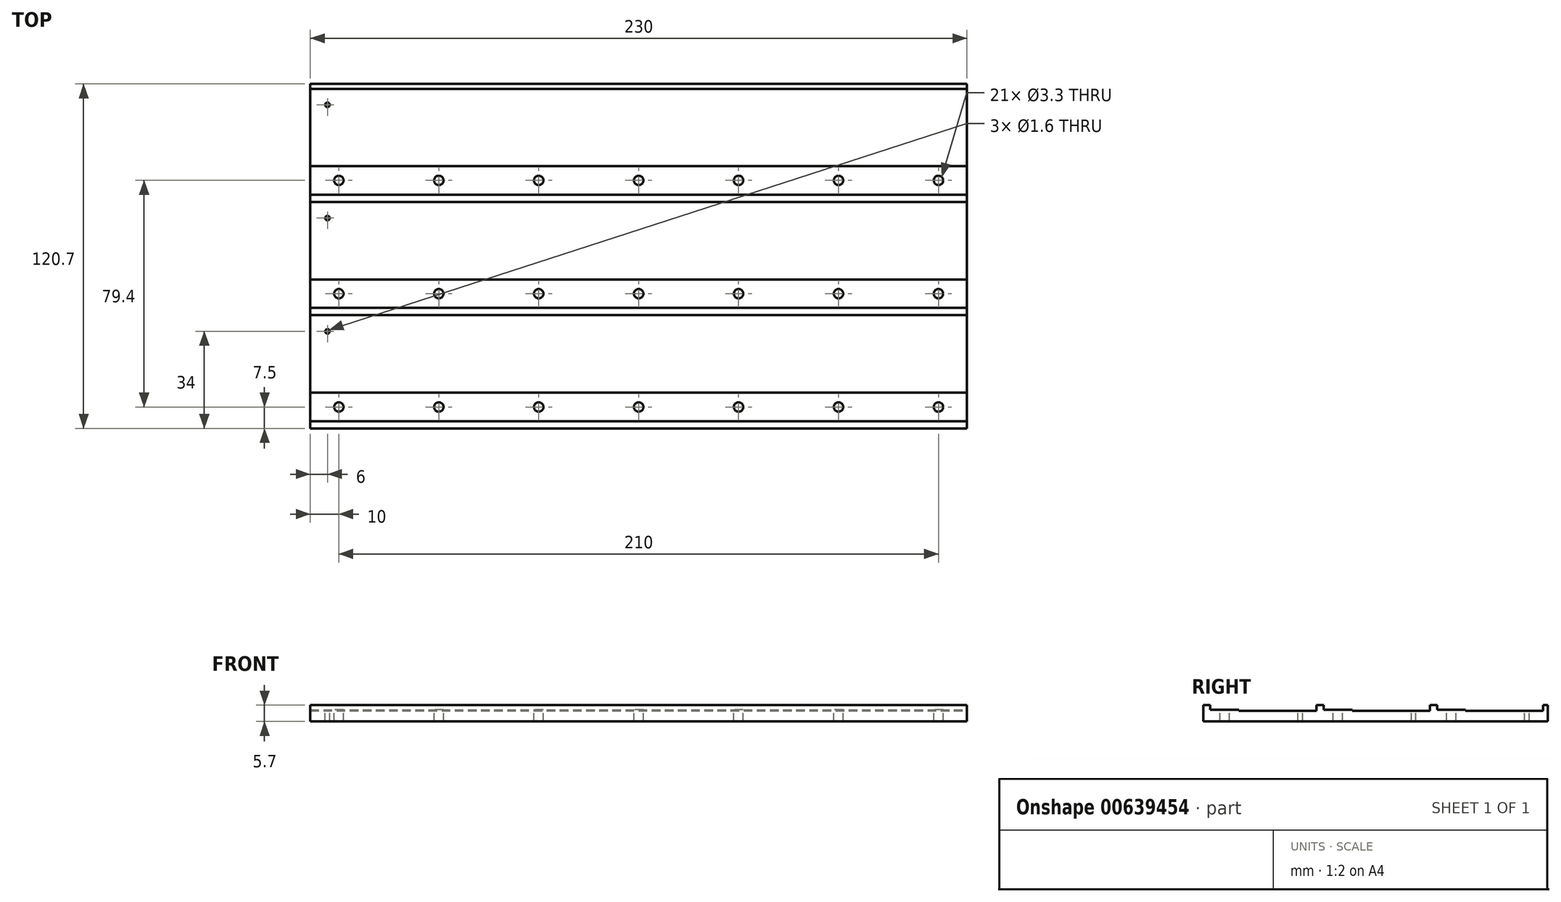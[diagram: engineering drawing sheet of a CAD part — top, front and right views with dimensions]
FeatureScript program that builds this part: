
annotation { "Feature Type Name" : "Feature", "Feature Type Description" : "" }
export const myFeature = defineFeature(function(context is Context, id is Id, definition is map)
    precondition{}
    {
        {
            var Q0;
            Q0=qCreatedBy(makeId("Top.planeOp"),FACE);
            var sketch = newSketch(context, id + "F0", { "sketchPlane" : qUnion([Q0])});
            skLineSegment(sketch, "E0.bottom", {"start": v(115, 60.35) * mm, "end": v(-115, 60.35) * mm});
            skLineSegment(sketch, "E0.top", {"start": v(115, -60.35) * mm, "end": v(-115, -60.35) * mm});
            skLineSegment(sketch, "E0.left", {"start": v(115, 60.35) * mm, "end": v(115, -60.35) * mm});
            skLineSegment(sketch, "E0.right", {"start": v(-115, 60.35) * mm, "end": v(-115, -60.35) * mm});
            skPoint(sketch, "E0.middle", {"position": v(0, 0) * mm});
            skSolve(sketch);
        }
        {
            var Q0;
            Q0=makeQuery(id+"F0.imprint","IMPRINT",FACE,{"disambiguationData":[TD([[makeQuery(id+"F0.imprint","IMPRINT",EDGE,{"derivedFrom":sQuery(id+"F0.wireOp",EDGE,"E0.bottom")}),1.0]])]});
            extrude(context, id + "F1", {"entities" : qUnion([Q0]), "depth" : 3.7 * mm, "offsetDistance" : 25 * mm});
        }
        {
            var Q0;
            Q0=makeQuery(id+"F1.opExtrude","CAP_FACE",FACE,{"disambiguationData":[OSD([sQuery(id+"F0.wireOp",EDGE,"E0.bottom"),sQuery(id+"F0.wireOp",EDGE,"E0.top"),sQuery(id+"F0.wireOp",EDGE,"E0.left"),sQuery(id+"F0.wireOp",EDGE,"E0.right")])],"isStart":false});
            var sketch = newSketch(context, id + "F2", { "sketchPlane" : qUnion([Q0])});
            skLineSegment(sketch, "E1.bottom", {"start": v(-115, 60.35) * mm, "end": v(115, 60.35) * mm});
            skLineSegment(sketch, "E1.top", {"start": v(-115, 58.65) * mm, "end": v(115, 58.65) * mm});
            skLineSegment(sketch, "E1.left", {"start": v(-115, 60.35) * mm, "end": v(-115, 58.65) * mm});
            skLineSegment(sketch, "E1.right", {"start": v(115, 60.35) * mm, "end": v(115, 58.65) * mm});
            skLineSegment(sketch, "E2.bottom", {"start": v(-115, 19.05) * mm, "end": v(115, 19.05) * mm});
            skLineSegment(sketch, "E2.top", {"start": v(-115, 21.55) * mm, "end": v(115, 21.55) * mm});
            skLineSegment(sketch, "E2.left", {"start": v(-115, 19.05) * mm, "end": v(-115, 21.55) * mm});
            skLineSegment(sketch, "E2.right", {"start": v(115, 19.05) * mm, "end": v(115, 21.55) * mm});
            skLineSegment(sketch, "E3.bottom", {"start": v(-115, -18.15) * mm, "end": v(115, -18.15) * mm});
            skLineSegment(sketch, "E3.top", {"start": v(-115, -20.65) * mm, "end": v(115, -20.65) * mm});
            skLineSegment(sketch, "E3.left", {"start": v(-115, -18.15) * mm, "end": v(-115, -20.65) * mm});
            skLineSegment(sketch, "E3.right", {"start": v(115, -18.15) * mm, "end": v(115, -20.65) * mm});
            skLineSegment(sketch, "E4.bottom", {"start": v(-115, -57.85) * mm, "end": v(115, -57.85) * mm});
            skLineSegment(sketch, "E4.top", {"start": v(-115, -60.35) * mm, "end": v(115, -60.35) * mm});
            skLineSegment(sketch, "E4.left", {"start": v(-115, -57.85) * mm, "end": v(-115, -60.35) * mm});
            skLineSegment(sketch, "E4.right", {"start": v(115, -57.85) * mm, "end": v(115, -60.35) * mm});
            skSolve(sketch);
        }
        {
            var Q0;
            Q0=makeQuery(id+"F2.imprint","IMPRINT",FACE,{"disambiguationData":[TD([[makeQuery(id+"F2.imprint","IMPRINT",EDGE,{"derivedFrom":sQuery(id+"F2.wireOp",EDGE,"E1.bottom")}),1.0]])]});
            var Q1;
            Q1=makeQuery(id+"F2.imprint","IMPRINT",FACE,{"disambiguationData":[TD([[makeQuery(id+"F2.imprint","IMPRINT",EDGE,{"derivedFrom":sQuery(id+"F2.wireOp",EDGE,"E2.bottom")}),1.0]])]});
            var Q2;
            Q2=makeQuery(id+"F2.imprint","IMPRINT",FACE,{"disambiguationData":[TD([[makeQuery(id+"F2.imprint","IMPRINT",EDGE,{"derivedFrom":sQuery(id+"F2.wireOp",EDGE,"E3.bottom")}),-1.0]])]});
            var Q3;
            Q3=makeQuery(id+"F2.imprint","IMPRINT",FACE,{"disambiguationData":[TD([[makeQuery(id+"F2.imprint","IMPRINT",EDGE,{"derivedFrom":sQuery(id+"F2.wireOp",EDGE,"E4.bottom")}),-1.0]])]});
            extrude(context, id + "F3", {"entities" : qUnion([Q0, Q1, Q2, Q3]), "operationType" : NewBodyOperationType.ADD, "depth" : 2 * mm, "offsetDistance" : 25 * mm});
        }
        {
            var Q0;
            {var subQ0=sQuery(id+"F0.wireOp",EDGE,"E0.left");var subQ1=sQuery(id+"F0.wireOp",EDGE,"E0.right");Q0=makeQuery(id+"F3.boolean.opBoolean","SPLIT",FACE,{"disambiguationData":[TD([makeQuery(id+"F3.opExtrude","SWEPT_FACE",FACE,{"disambiguationData":[OSD([sQuery(id+"F2.wireOp",EDGE,"E1.top")])]})])],"derivedFrom":makeQuery(id+"F1.opExtrude","CAP_FACE",FACE,{"disambiguationData":[OSD([sQuery(id+"F0.wireOp",EDGE,"E0.bottom"),sQuery(id+"F0.wireOp",EDGE,"E0.top"),subQ0,subQ1])],"isStart":false})});}
            var sketch = newSketch(context, id + "F4", { "sketchPlane" : qUnion([Q0])});
            skLineSegment(sketch, "E5.bottom", {"start": v(-115, 21.55) * mm, "end": v(115, 21.55) * mm});
            skLineSegment(sketch, "E5.top", {"start": v(-115, 31.55) * mm, "end": v(115, 31.55) * mm});
            skLineSegment(sketch, "E5.left", {"start": v(-115, 21.55) * mm, "end": v(-115, 31.55) * mm});
            skLineSegment(sketch, "E5.right", {"start": v(115, 21.55) * mm, "end": v(115, 31.55) * mm});
            skSolve(sketch);
        }
        {
            var Q0;
            Q0=makeQuery(id+"F4.imprint","IMPRINT",FACE,{"disambiguationData":[TD([[makeQuery(id+"F4.imprint","IMPRINT",EDGE,{"derivedFrom":sQuery(id+"F4.wireOp",EDGE,"E5.bottom")}),1.0]])]});
            extrude(context, id + "F5", {"entities" : qUnion([Q0]), "operationType" : NewBodyOperationType.ADD, "depth" : 0.4 * mm, "offsetDistance" : 25 * mm});
        }
        {
            var Q0;
            {var subQ0=sQuery(id+"F0.wireOp",EDGE,"E0.left");var subQ1=sQuery(id+"F0.wireOp",EDGE,"E0.right");Q0=makeQuery(id+"F3.boolean.opBoolean","SPLIT",FACE,{"disambiguationData":[TD([makeQuery(id+"F3.opExtrude","SWEPT_FACE",FACE,{"disambiguationData":[OSD([sQuery(id+"F2.wireOp",EDGE,"E2.bottom")])]})])],"derivedFrom":makeQuery(id+"F1.opExtrude","CAP_FACE",FACE,{"disambiguationData":[OSD([sQuery(id+"F0.wireOp",EDGE,"E0.bottom"),sQuery(id+"F0.wireOp",EDGE,"E0.top"),subQ0,subQ1])],"isStart":false})});}
            var sketch = newSketch(context, id + "F6", { "sketchPlane" : qUnion([Q0])});
            skLineSegment(sketch, "E6.bottom", {"start": v(-115, -18.15) * mm, "end": v(115, -18.15) * mm});
            skLineSegment(sketch, "E6.top", {"start": v(-115, -8.15) * mm, "end": v(115, -8.15) * mm});
            skLineSegment(sketch, "E6.left", {"start": v(-115, -18.15) * mm, "end": v(-115, -8.15) * mm});
            skLineSegment(sketch, "E6.right", {"start": v(115, -18.15) * mm, "end": v(115, -8.15) * mm});
            skSolve(sketch);
        }
        {
            var Q0;
            Q0=makeQuery(id+"F6.imprint","IMPRINT",FACE,{"disambiguationData":[TD([[makeQuery(id+"F6.imprint","IMPRINT",EDGE,{"derivedFrom":sQuery(id+"F6.wireOp",EDGE,"E6.bottom")}),1.0]])]});
            extrude(context, id + "F7", {"entities" : qUnion([Q0]), "operationType" : NewBodyOperationType.ADD, "depth" : 0.4 * mm, "offsetDistance" : 25 * mm});
        }
        {
            var Q0;
            {var subQ0=sQuery(id+"F0.wireOp",EDGE,"E0.left");var subQ1=sQuery(id+"F0.wireOp",EDGE,"E0.right");Q0=makeQuery(id+"F3.boolean.opBoolean","SPLIT",FACE,{"disambiguationData":[TD([makeQuery(id+"F3.opExtrude","SWEPT_FACE",FACE,{"disambiguationData":[OSD([sQuery(id+"F2.wireOp",EDGE,"E3.top")])]})])],"derivedFrom":makeQuery(id+"F1.opExtrude","CAP_FACE",FACE,{"disambiguationData":[OSD([sQuery(id+"F0.wireOp",EDGE,"E0.bottom"),sQuery(id+"F0.wireOp",EDGE,"E0.top"),subQ0,subQ1])],"isStart":false})});}
            var sketch = newSketch(context, id + "F8", { "sketchPlane" : qUnion([Q0])});
            skLineSegment(sketch, "E7.bottom", {"start": v(-115, -57.85) * mm, "end": v(115, -57.85) * mm});
            skLineSegment(sketch, "E7.top", {"start": v(-115, -47.85) * mm, "end": v(115, -47.85) * mm});
            skLineSegment(sketch, "E7.left", {"start": v(-115, -57.85) * mm, "end": v(-115, -47.85) * mm});
            skLineSegment(sketch, "E7.right", {"start": v(115, -57.85) * mm, "end": v(115, -47.85) * mm});
            skSolve(sketch);
        }
        {
            var Q0;
            Q0=makeQuery(id+"F8.imprint","IMPRINT",FACE,{"disambiguationData":[TD([[makeQuery(id+"F8.imprint","IMPRINT",EDGE,{"derivedFrom":sQuery(id+"F8.wireOp",EDGE,"E7.bottom")}),1.0]])]});
            extrude(context, id + "F9", {"entities" : qUnion([Q0]), "operationType" : NewBodyOperationType.ADD, "depth" : 0.4 * mm, "offsetDistance" : 25 * mm});
        }
        {
            var Q0;
            Q0=makeQuery(id+"F5.opExtrude","CAP_FACE",FACE,{"disambiguationData":[OSD([sQuery(id+"F4.wireOp",EDGE,"E5.bottom"),sQuery(id+"F4.wireOp",EDGE,"E5.top"),sQuery(id+"F4.wireOp",EDGE,"E5.left"),sQuery(id+"F4.wireOp",EDGE,"E5.right")])],"isStart":false});
            var sketch = newSketch(context, id + "F10", { "sketchPlane" : qUnion([Q0])});
            skPoint(sketch, "E8", {"position": v(-105, 26.55) * mm});
            skPoint(sketch, "E8.positionSnap0", {"position": v(-115, 26.55) * mm});
            skPoint(sketch, "E9", {"position": v(-70, 26.55) * mm});
            skPoint(sketch, "E10", {"position": v(-35, 26.55) * mm});
            skPoint(sketch, "E11", {"position": v(0, 26.55) * mm});
            skPoint(sketch, "E12", {"position": v(35, 26.55) * mm});
            skPoint(sketch, "E13", {"position": v(70, 26.55) * mm});
            skPoint(sketch, "E14", {"position": v(105, 26.55) * mm});
            skSolve(sketch);
        }
        {
            var Q0;
            Q0=sQuery(id+"F10.wireOp",VERTEX,"E8");
            var Q1;
            Q1=sQuery(id+"F10.wireOp",VERTEX,"E9");
            var Q2;
            Q2=sQuery(id+"F10.wireOp",VERTEX,"E10");
            var Q3;
            Q3=sQuery(id+"F10.wireOp",VERTEX,"E11");
            var Q4;
            Q4=sQuery(id+"F10.wireOp",VERTEX,"E12");
            var Q5;
            Q5=sQuery(id+"F10.wireOp",VERTEX,"E13");
            var Q6;
            Q6=sQuery(id+"F10.wireOp",VERTEX,"E14");
            var Q7;
            Q7=makeQuery(id+"F1.opExtrude","SWEPT_BODY",BODY,{"disambiguationData":[OSD([sQuery(id+"F0.wireOp",EDGE,"E0.bottom"),sQuery(id+"F0.wireOp",EDGE,"E0.top"),sQuery(id+"F0.wireOp",EDGE,"E0.left"),sQuery(id+"F0.wireOp",EDGE,"E0.right")])]});
            hole(context, id + "F11", {"style" : HoleStyle.SIMPLE, "endStyle" : HoleEndStyle.THROUGH, "standardTappedOrClearance" : lookupTablePath({ "standard" : "ISO", "fit" : "Normal", "size" : "M3", "type" : "Clearance" }), "standardBlindInLast" : lookupTablePath({ "fit" : "Standard", "standard" : "ISO", "size" : "M3", "type" : "Clearance" }), "holeDiameter" : 3.3 * mm, "majorDiameter" : 5 * mm, "isTappedThrough" : true, "tappedDepth" : 12 * mm, "tapClearance" : 3, "locations" : qUnion([Q0, Q1, Q2, Q3, Q4, Q5, Q6]), "scope" : qUnion([Q7])});
        }
        {
            var Q0;
            Q0=makeQuery(id+"F7.opExtrude","CAP_FACE",FACE,{"disambiguationData":[OSD([sQuery(id+"F6.wireOp",EDGE,"E6.bottom"),sQuery(id+"F6.wireOp",EDGE,"E6.top"),sQuery(id+"F6.wireOp",EDGE,"E6.left"),sQuery(id+"F6.wireOp",EDGE,"E6.right")])],"isStart":false});
            var sketch = newSketch(context, id + "F12", { "sketchPlane" : qUnion([Q0])});
            skPoint(sketch, "E15", {"position": v(-105, -13.15) * mm});
            skPoint(sketch, "E15.positionSnap0", {"position": v(-115, -13.15) * mm});
            skPoint(sketch, "E16", {"position": v(-70, -13.15) * mm});
            skPoint(sketch, "E17", {"position": v(-35, -13.15) * mm});
            skPoint(sketch, "E18", {"position": v(0, -13.15) * mm});
            skPoint(sketch, "E19", {"position": v(35, -13.15) * mm});
            skPoint(sketch, "E20", {"position": v(70, -13.15) * mm});
            skPoint(sketch, "E21", {"position": v(105, -13.15) * mm});
            skSolve(sketch);
        }
        {
            var Q0;
            Q0=sQuery(id+"F12.wireOp",VERTEX,"E15");
            var Q1;
            Q1=sQuery(id+"F12.wireOp",VERTEX,"E16");
            var Q2;
            Q2=sQuery(id+"F12.wireOp",VERTEX,"E17");
            var Q3;
            Q3=sQuery(id+"F12.wireOp",VERTEX,"E18");
            var Q4;
            Q4=sQuery(id+"F12.wireOp",VERTEX,"E19");
            var Q5;
            Q5=sQuery(id+"F12.wireOp",VERTEX,"E20");
            var Q6;
            Q6=sQuery(id+"F12.wireOp",VERTEX,"E21");
            var Q7;
            Q7=makeQuery(id+"F1.opExtrude","SWEPT_BODY",BODY,{"disambiguationData":[OSD([sQuery(id+"F0.wireOp",EDGE,"E0.bottom"),sQuery(id+"F0.wireOp",EDGE,"E0.top"),sQuery(id+"F0.wireOp",EDGE,"E0.left"),sQuery(id+"F0.wireOp",EDGE,"E0.right")])]});
            hole(context, id + "F13", {"style" : HoleStyle.SIMPLE, "endStyle" : HoleEndStyle.THROUGH, "standardTappedOrClearance" : lookupTablePath({ "standard" : "ISO", "fit" : "Normal", "size" : "M3", "type" : "Clearance" }), "standardBlindInLast" : lookupTablePath({ "fit" : "Standard", "standard" : "ISO", "size" : "M3", "type" : "Clearance" }), "holeDiameter" : 3.3 * mm, "majorDiameter" : 5 * mm, "isTappedThrough" : true, "tappedDepth" : 12 * mm, "tapClearance" : 3, "locations" : qUnion([Q0, Q1, Q2, Q3, Q4, Q5, Q6]), "scope" : qUnion([Q7])});
        }
        {
            var Q0;
            Q0=makeQuery(id+"F9.opExtrude","CAP_FACE",FACE,{"disambiguationData":[OSD([sQuery(id+"F8.wireOp",EDGE,"E7.bottom"),sQuery(id+"F8.wireOp",EDGE,"E7.top"),sQuery(id+"F8.wireOp",EDGE,"E7.left"),sQuery(id+"F8.wireOp",EDGE,"E7.right")])],"isStart":false});
            var sketch = newSketch(context, id + "F14", { "sketchPlane" : qUnion([Q0])});
            skPoint(sketch, "E22", {"position": v(-105, -52.85) * mm});
            skPoint(sketch, "E22.positionSnap0", {"position": v(-115, -52.85) * mm});
            skPoint(sketch, "E23", {"position": v(-70, -52.85) * mm});
            skPoint(sketch, "E24", {"position": v(-35, -52.85) * mm});
            skPoint(sketch, "E25", {"position": v(0, -52.85) * mm});
            skPoint(sketch, "E26", {"position": v(35, -52.85) * mm});
            skPoint(sketch, "E27", {"position": v(70, -52.85) * mm});
            skPoint(sketch, "E28", {"position": v(105, -52.85) * mm});
            skSolve(sketch);
        }
        {
            var Q0;
            Q0=sQuery(id+"F14.wireOp",VERTEX,"E22");
            var Q1;
            Q1=sQuery(id+"F14.wireOp",VERTEX,"E23");
            var Q2;
            Q2=sQuery(id+"F14.wireOp",VERTEX,"E24");
            var Q3;
            Q3=sQuery(id+"F14.wireOp",VERTEX,"E25");
            var Q4;
            Q4=sQuery(id+"F14.wireOp",VERTEX,"E26");
            var Q5;
            Q5=sQuery(id+"F14.wireOp",VERTEX,"E27");
            var Q6;
            Q6=sQuery(id+"F14.wireOp",VERTEX,"E28");
            var Q7;
            Q7=makeQuery(id+"F1.opExtrude","SWEPT_BODY",BODY,{"disambiguationData":[OSD([sQuery(id+"F0.wireOp",EDGE,"E0.bottom"),sQuery(id+"F0.wireOp",EDGE,"E0.top"),sQuery(id+"F0.wireOp",EDGE,"E0.left"),sQuery(id+"F0.wireOp",EDGE,"E0.right")])]});
            hole(context, id + "F15", {"style" : HoleStyle.SIMPLE, "endStyle" : HoleEndStyle.THROUGH, "standardTappedOrClearance" : lookupTablePath({ "standard" : "ISO", "fit" : "Normal", "size" : "M3", "type" : "Clearance" }), "standardBlindInLast" : lookupTablePath({ "fit" : "Standard", "standard" : "ISO", "size" : "M3", "type" : "Clearance" }), "holeDiameter" : 3.3 * mm, "majorDiameter" : 5 * mm, "isTappedThrough" : true, "tappedDepth" : 12 * mm, "tapClearance" : 3, "locations" : qUnion([Q0, Q1, Q2, Q3, Q4, Q5, Q6]), "scope" : qUnion([Q7])});
        }
        {
            var Q0;
            {var subQ0=sQuery(id+"F0.wireOp",EDGE,"E0.left");var subQ1=sQuery(id+"F0.wireOp",EDGE,"E0.right");Q0=makeQuery(id+"F3.boolean.opBoolean","SPLIT",FACE,{"disambiguationData":[TD([makeQuery(id+"F3.opExtrude","SWEPT_FACE",FACE,{"disambiguationData":[OSD([sQuery(id+"F2.wireOp",EDGE,"E1.top")])]})])],"derivedFrom":makeQuery(id+"F1.opExtrude","CAP_FACE",FACE,{"disambiguationData":[OSD([sQuery(id+"F0.wireOp",EDGE,"E0.bottom"),sQuery(id+"F0.wireOp",EDGE,"E0.top"),subQ0,subQ1])],"isStart":false})});}
            var sketch = newSketch(context, id + "F16", { "sketchPlane" : qUnion([Q0])});
            skPoint(sketch, "E29", {"position": v(-109, 53.05) * mm});
            skSolve(sketch);
        }
        {
            var Q0;
            Q0=sQuery(id+"F16.wireOp",VERTEX,"E29");
            var Q1;
            Q1=makeQuery(id+"F1.opExtrude","SWEPT_BODY",BODY,{"disambiguationData":[OSD([sQuery(id+"F0.wireOp",EDGE,"E0.bottom"),sQuery(id+"F0.wireOp",EDGE,"E0.top"),sQuery(id+"F0.wireOp",EDGE,"E0.left"),sQuery(id+"F0.wireOp",EDGE,"E0.right")])]});
            hole(context, id + "F17", {"style" : HoleStyle.SIMPLE, "endStyle" : HoleEndStyle.THROUGH, "holeDiameter" : 1.6 * mm, "majorDiameter" : 5 * mm, "isTappedThrough" : true, "tappedDepth" : 12 * mm, "tapClearance" : 3, "locations" : qUnion([Q0]), "scope" : qUnion([Q1])});
        }
        {
            var Q0;
            {var subQ0=sQuery(id+"F0.wireOp",EDGE,"E0.left");var subQ1=sQuery(id+"F0.wireOp",EDGE,"E0.right");Q0=makeQuery(id+"F3.boolean.opBoolean","SPLIT",FACE,{"disambiguationData":[TD([makeQuery(id+"F3.opExtrude","SWEPT_FACE",FACE,{"disambiguationData":[OSD([sQuery(id+"F2.wireOp",EDGE,"E2.bottom")])]})])],"derivedFrom":makeQuery(id+"F1.opExtrude","CAP_FACE",FACE,{"disambiguationData":[OSD([sQuery(id+"F0.wireOp",EDGE,"E0.bottom"),sQuery(id+"F0.wireOp",EDGE,"E0.top"),subQ0,subQ1])],"isStart":false})});}
            var sketch = newSketch(context, id + "F18", { "sketchPlane" : qUnion([Q0])});
            skPoint(sketch, "E30", {"position": v(-109, 13.35) * mm});
            skSolve(sketch);
        }
        {
            var Q0;
            Q0=sQuery(id+"F18.wireOp",VERTEX,"E30");
            var Q1;
            Q1=makeQuery(id+"F1.opExtrude","SWEPT_BODY",BODY,{"disambiguationData":[OSD([sQuery(id+"F0.wireOp",EDGE,"E0.bottom"),sQuery(id+"F0.wireOp",EDGE,"E0.top"),sQuery(id+"F0.wireOp",EDGE,"E0.left"),sQuery(id+"F0.wireOp",EDGE,"E0.right")])]});
            hole(context, id + "F19", {"style" : HoleStyle.SIMPLE, "endStyle" : HoleEndStyle.THROUGH, "holeDiameter" : 1.6 * mm, "majorDiameter" : 5 * mm, "isTappedThrough" : true, "tappedDepth" : 12 * mm, "tapClearance" : 3, "locations" : qUnion([Q0]), "scope" : qUnion([Q1])});
        }
        {
            var Q0;
            {var subQ0=sQuery(id+"F0.wireOp",EDGE,"E0.left");var subQ1=sQuery(id+"F0.wireOp",EDGE,"E0.right");Q0=makeQuery(id+"F3.boolean.opBoolean","SPLIT",FACE,{"disambiguationData":[TD([makeQuery(id+"F3.opExtrude","SWEPT_FACE",FACE,{"disambiguationData":[OSD([sQuery(id+"F2.wireOp",EDGE,"E3.top")])]})])],"derivedFrom":makeQuery(id+"F1.opExtrude","CAP_FACE",FACE,{"disambiguationData":[OSD([sQuery(id+"F0.wireOp",EDGE,"E0.bottom"),sQuery(id+"F0.wireOp",EDGE,"E0.top"),subQ0,subQ1])],"isStart":false})});}
            var sketch = newSketch(context, id + "F20", { "sketchPlane" : qUnion([Q0])});
            skPoint(sketch, "E31", {"position": v(-109, -26.35) * mm});
            skSolve(sketch);
        }
        {
            var Q0;
            Q0=sQuery(id+"F20.wireOp",VERTEX,"E31");
            var Q1;
            Q1=makeQuery(id+"F1.opExtrude","SWEPT_BODY",BODY,{"disambiguationData":[OSD([sQuery(id+"F0.wireOp",EDGE,"E0.bottom"),sQuery(id+"F0.wireOp",EDGE,"E0.top"),sQuery(id+"F0.wireOp",EDGE,"E0.left"),sQuery(id+"F0.wireOp",EDGE,"E0.right")])]});
            hole(context, id + "F21", {"style" : HoleStyle.SIMPLE, "endStyle" : HoleEndStyle.THROUGH, "holeDiameter" : 1.6 * mm, "majorDiameter" : 5 * mm, "isTappedThrough" : true, "tappedDepth" : 12 * mm, "tapClearance" : 3, "locations" : qUnion([Q0]), "scope" : qUnion([Q1])});
        }
    });
